# Revit family: 2069400 Sylvania Lighting Fixture PIXER RECESSED 1200X300 HE 4P 4000K9 SSC01
name_source: partatom
category: Lighting Fixtures
revit_build: Autodesk Revit 2016 (Build: 20150220_1215(x64)
units: mm (PartAtom-declared; Revit-internal decimal feet)

## family parameters
Cut with Voids When Loaded = No
Host = Face
Light Source = No
OmniClass Number = 23.80.70.00
OmniClass Title = Lighting
Part Type = Normal
Room Calculation Point = No
Round Connector Dimension = Use Diameter
Shared = No

## types (1)
- 2069400 PIXER R 1200 HE 4P 4K9 SSC01
    Apparent Load = 26 VA
    Assembly Code = D5020200
    AssetType = Fixed
    ClassificationName = Uniclass2015
    ClassificationValue = EF_70_80
    Cost = 0 $
    Default Elevation = 1219 mm
    Description = PIXER RECESSED 1200X300 HE 4P 4000K9 SSC01 is a high performance low glare office luminaire with individually adjustable light pods to enhance arhitectural design. Diffuser is made of optical grade polycarbonate with an optical film for high efficacy and excellent glare control. Suitable for offices where aesthetics is important. Ceiling recessed 1200x300mm, White colour - RAL9010. SylSmart stand alone office capable, 4000K Neutral White LED, CRI>90, chromaticity tolerance of 3-step MacAdam ellipse. Lumen package of 3280 lm, total power consumtion 26W, efficacy 126lm/W. Lumen maintenance of L90B10 at 61,000 hours. UGR<19. IK02, IP20. Electrical protection: Class II. Glow wire test 650°C.
    DocumentationLiterature = http://www.sylvania-lighting.com
    ElectricShockClassification = Class II
    IfcExportAs = IfcLightFixtureType
    IfcExportType = IfcLightFixtureType
    ImpactProtectionIndex = IK02
    IngressProtection = IP20
    Keynote = 16500
    Lamp = LED
    LampColourRenderingIndex = 90
    LampColourTemperature = 4000 K
    LampMacAdamStep = 3
    LampNominalLuminous = 3283 lm
    LampsType = LED
    LengthPods_SYL = 1150 mm  [stored 3.77297 ft]
    Length_SYL = 1195 mm  [stored 3.9206 ft]
    LightOutputRatio = 100
    LuminousEfficacy = 126 lm/W
    Manufacturer = Feilo Sylvania
    ManufacturerName = Feilo Sylvania
    Material = powder coated steel housing, polycarbonate diffuser
    Material_1_SYL = PC/ABS Plastic
    Model = PIXER RECESSED 1200X300 HE 4P 4000K9 SSC01
    ModelNumber = 2069400
    ModelReference = PIXER RECESSED 1200X300 HE 4P 4000K9 SSC01
    Name = PIXER RECESSED 1200X300 HE 4P 4000K9 SSC01
    NominalDepth = 295 mm  [stored 0.967848 ft]
    NominalHeight = 75 mm
    NominalLength = 1195 mm  [stored 3.9206 ft]
    PodXInstance_SYL = 4
    PowerConsumption = 26 W
    PowerFactor = 0
    RadiusBody_SYL = 5 mm  [stored 0.0164042 ft]
    Type Image = <None>
    TypeName = PIXER RECESSED 1200X300 HE 4P 4000K9 SSC01
    TypePodRect_SYL = Pixer Pod Rectangular : 2069400 PIXER R 1200 HE 4P 4K9 SSC01
    URL = http://www.sylvania-lighting.com
    Voltage = 0 V
    Weight = 6.0 kg
    Width_SYL = 295 mm  [stored 0.967848 ft]
    Xdistance_SYL = 144 mm
    Xinstance_SYL = 8
    Ydistance_SYL = 148 mm
    Yinstance_SYL = 2

note: [stored X ft] marks values corroborated as IEEE doubles in the binary element streams (Revit-internal decimal feet)

## geometry (parser evidence)
native form markers: Sweep x4
no freeform markers — native parametric forms only
